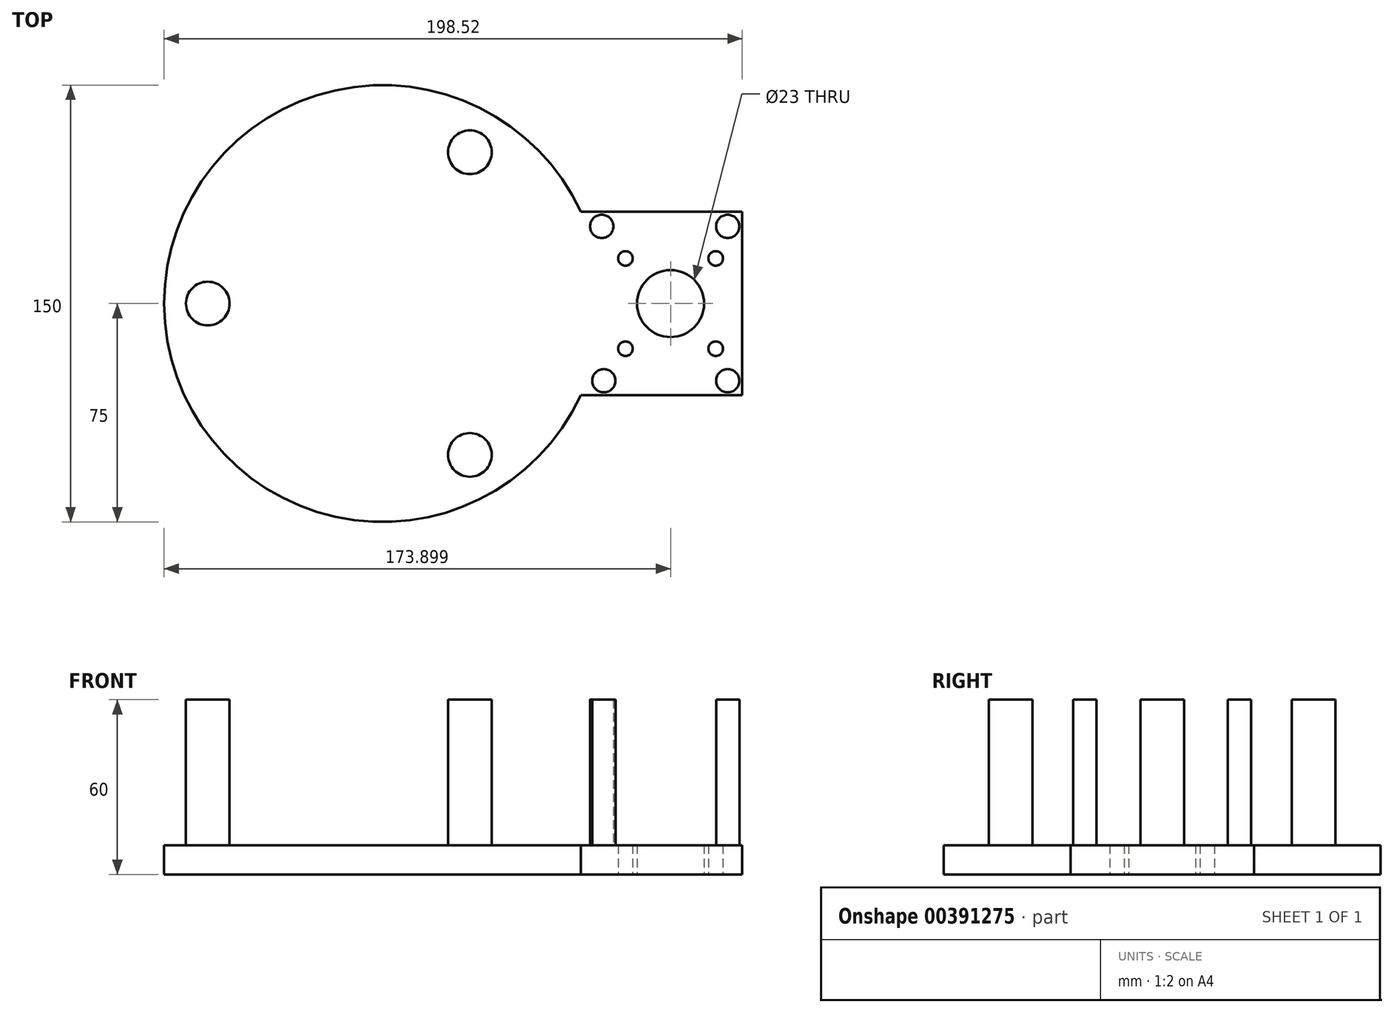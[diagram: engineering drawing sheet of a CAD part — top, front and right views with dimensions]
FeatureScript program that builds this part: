
annotation { "Feature Type Name" : "Feature", "Feature Type Description" : "" }
export const myFeature = defineFeature(function(context is Context, id is Id, definition is map)
    precondition{}
    {
        {
            var Q0;
            Q0=qCreatedBy(makeId("Top.planeOp"),FACE);
            var sketch = newSketch(context, id + "F0", { "sketchPlane" : qUnion([Q0])});
            skCircle(sketch, "E0", {"center": v(0, 0) * mm, "radius": 75 * mm});
            skLineSegment(sketch, "E1.bottom", {"start": v(123.52, -31.5) * mm, "end": v(70.52, -31.5) * mm, "construction": true});
            skLineSegment(sketch, "E1.top", {"start": v(123.52, 31.5) * mm, "end": v(70.52, 31.5) * mm, "construction": true});
            skLineSegment(sketch, "E1.left", {"start": v(123.52, -31.5) * mm, "end": v(123.52, 31.5) * mm, "construction": true});
            skLineSegment(sketch, "E1.right", {"start": v(70.52, -31.5) * mm, "end": v(70.52, 31.5) * mm, "construction": true});
            skPoint(sketch, "E1.middle", {"position": v(97.02, 0) * mm});
            skLineSegment(sketch, "E2", {"start": v(68.06, 31.5) * mm, "end": v(123.52, 31.5) * mm});
            skLineSegment(sketch, "E3", {"start": v(68.06, -31.5) * mm, "end": v(123.52, -31.5) * mm});
            skLineSegment(sketch, "E4", {"start": v(123.52, 31.5) * mm, "end": v(123.52, -31.5) * mm});
            skSolve(sketch);
        }
        {
            var Q0;
            {var subQ0=sQuery(id+"F0.wireOp",EDGE,"E0");var subQ1=makeQuery(id+"F0.imprint","INTERSECT",VERTEX,{"derivedFrom":[subQ0,sQuery(id+"F0.wireOp",EDGE,"E2")]});Q0=makeQuery(id+"F0.imprint","IMPRINT",FACE,{"disambiguationData":[TD([[makeQuery(id+"F0.imprint","IMPRINT",EDGE,{"disambiguationData":[TD([[subQ1,-1.0]])],"derivedFrom":subQ0}),1.0]])]});}
            var Q1;
            {var subQ0=sQuery(id+"F0.wireOp",EDGE,"E2");Q1=makeQuery(id+"F0.imprint","IMPRINT",FACE,{"disambiguationData":[TD([[makeQuery(id+"F0.imprint","IMPRINT",EDGE,{"derivedFrom":subQ0}),-1.0]])]});}
            extrude(context, id + "F1", {"entities" : qUnion([Q0, Q1]), "depth" : 10 * mm});
        }
        {
            var Q0;
            {var subQ0=sQuery(id+"F0.wireOp",EDGE,"E2");Q0=makeQuery(id+"F0.imprint","IMPRINT",FACE,{"disambiguationData":[TD([[makeQuery(id+"F0.imprint","IMPRINT",EDGE,{"derivedFrom":subQ0}),-1.0]])]});}
            var sketch = newSketch(context, id + "F2", { "sketchPlane" : qUnion([Q0])});
            skLineSegment(sketch, "E5.bottom", {"start": v(83.4, -15.5) * mm, "end": v(114.4, -15.5) * mm, "construction": true});
            skLineSegment(sketch, "E5.top", {"start": v(83.4, 15.5) * mm, "end": v(114.4, 15.5) * mm, "construction": true});
            skLineSegment(sketch, "E5.left", {"start": v(83.4, -15.5) * mm, "end": v(83.4, 15.5) * mm, "construction": true});
            skLineSegment(sketch, "E5.right", {"start": v(114.4, -15.5) * mm, "end": v(114.4, 15.5) * mm, "construction": true});
            skPoint(sketch, "E5.middle", {"position": v(98.9, 0) * mm});
            skCircle(sketch, "E6", {"center": v(114.4, 15.5) * mm, "radius": 2.5 * mm});
            skCircle(sketch, "E7", {"center": v(83.4, 15.5) * mm, "radius": 2.5 * mm});
            skCircle(sketch, "E8", {"center": v(83.4, -15.5) * mm, "radius": 2.5 * mm});
            skCircle(sketch, "E9", {"center": v(114.4, -15.5) * mm, "radius": 2.5 * mm});
            skCircle(sketch, "E10", {"center": v(98.9, 0) * mm, "radius": 11.5 * mm});
            skSolve(sketch);
        }
        {
            var Q0;
            Q0=makeQuery(id+"F2.imprint","IMPRINT",FACE,{"disambiguationData":[TD([[makeQuery(id+"F2.imprint","IMPRINT",EDGE,{"derivedFrom":sQuery(id+"F2.wireOp",EDGE,"E6")}),1.0]])]});
            var Q1;
            Q1=makeQuery(id+"F2.imprint","IMPRINT",FACE,{"disambiguationData":[TD([[makeQuery(id+"F2.imprint","IMPRINT",EDGE,{"derivedFrom":sQuery(id+"F2.wireOp",EDGE,"E7")}),1.0]])]});
            var Q2;
            Q2=makeQuery(id+"F2.imprint","IMPRINT",FACE,{"disambiguationData":[TD([[makeQuery(id+"F2.imprint","IMPRINT",EDGE,{"derivedFrom":sQuery(id+"F2.wireOp",EDGE,"E8")}),1.0]])]});
            var Q3;
            Q3=makeQuery(id+"F2.imprint","IMPRINT",FACE,{"disambiguationData":[TD([[makeQuery(id+"F2.imprint","IMPRINT",EDGE,{"derivedFrom":sQuery(id+"F2.wireOp",EDGE,"E9")}),1.0]])]});
            var Q4;
            Q4=makeQuery(id+"F1.opExtrude","CAP_FACE",FACE,{"disambiguationData":[OSD([sQuery(id+"F0.wireOp",EDGE,"E0"),sQuery(id+"F0.wireOp",EDGE,"E2"),sQuery(id+"F0.wireOp",EDGE,"E3"),sQuery(id+"F0.wireOp",EDGE,"E4")])],"isStart":false});
            extrude(context, id + "F3", {"entities" : qUnion([Q0, Q1, Q2, Q3]), "operationType" : NewBodyOperationType.REMOVE, "endBound" : BoundingType.UP_TO_SURFACE, "endBoundEntityFace" : qUnion([Q4]), "depth" : 11 * mm});
        }
        {
            var Q0;
            Q0=makeQuery(id+"F2.imprint","IMPRINT",FACE,{"disambiguationData":[TD([[makeQuery(id+"F2.imprint","IMPRINT",EDGE,{"derivedFrom":sQuery(id+"F2.wireOp",EDGE,"E10")}),1.0]])]});
            var Q1;
            Q1=makeQuery(id+"F1.opExtrude","CAP_FACE",FACE,{"disambiguationData":[OSD([sQuery(id+"F0.wireOp",EDGE,"E0"),sQuery(id+"F0.wireOp",EDGE,"E2"),sQuery(id+"F0.wireOp",EDGE,"E3"),sQuery(id+"F0.wireOp",EDGE,"E4")])],"isStart":false});
            extrude(context, id + "F4", {"entities" : qUnion([Q0]), "operationType" : NewBodyOperationType.REMOVE, "endBound" : BoundingType.UP_TO_SURFACE, "endBoundEntityFace" : qUnion([Q1]), "depth" : 25 * mm});
        }
        {
            var Q0;
            Q0=makeQuery(id+"F1.opExtrude","CAP_FACE",FACE,{"disambiguationData":[OSD([sQuery(id+"F0.wireOp",EDGE,"E0"),sQuery(id+"F0.wireOp",EDGE,"E2"),sQuery(id+"F0.wireOp",EDGE,"E3"),sQuery(id+"F0.wireOp",EDGE,"E4")])],"isStart":false});
            var sketch = newSketch(context, id + "F5", { "sketchPlane" : qUnion([Q0])});
            skLineSegment(sketch, "E11.bottom", {"start": v(123.52, -31.5) * mm, "end": v(118.52, -31.5) * mm, "construction": true});
            skLineSegment(sketch, "E11.top", {"start": v(123.52, -26.5) * mm, "end": v(118.52, -26.5) * mm, "construction": true});
            skLineSegment(sketch, "E11.left", {"start": v(123.52, -31.5) * mm, "end": v(123.52, -26.5) * mm, "construction": true});
            skLineSegment(sketch, "E11.right", {"start": v(118.52, -31.5) * mm, "end": v(118.52, -26.5) * mm, "construction": true});
            skLineSegment(sketch, "E12.bottom", {"start": v(123.52, 31.5) * mm, "end": v(118.52, 31.5) * mm, "construction": true});
            skLineSegment(sketch, "E12.top", {"start": v(123.52, 26.5) * mm, "end": v(118.52, 26.5) * mm, "construction": true});
            skLineSegment(sketch, "E12.left", {"start": v(123.52, 31.5) * mm, "end": v(123.52, 26.5) * mm, "construction": true});
            skLineSegment(sketch, "E12.right", {"start": v(118.52, 31.5) * mm, "end": v(118.52, 26.5) * mm, "construction": true});
            skCircle(sketch, "E13", {"center": v(0, 0) * mm, "radius": 60 * mm, "construction": true});
            skLineSegment(sketch, "E14", {"start": v(75.26, 31.5) * mm, "end": v(75.26, 26.5) * mm, "construction": true});
            skLineSegment(sketch, "E15", {"start": v(75.97, -31.5) * mm, "end": v(75.97, -26.5) * mm, "construction": true});
            skCircle(sketch, "E16", {"center": v(-60, 0) * mm, "radius": 7.5 * mm});
            skCircle(sketch, "E17.1.0", {"center": v(30, -51.96) * mm, "radius": 7.5 * mm});
            skCircle(sketch, "E17.2.0", {"center": v(30, 51.96) * mm, "radius": 7.5 * mm});
            skCircle(sketch, "E18", {"center": v(75.26, 26.5) * mm, "radius": 4 * mm});
            skCircle(sketch, "E19", {"center": v(118.52, 26.5) * mm, "radius": 4 * mm});
            skCircle(sketch, "E20", {"center": v(118.52, -26.5) * mm, "radius": 4 * mm});
            skCircle(sketch, "E21", {"center": v(75.97, -26.5) * mm, "radius": 4 * mm});
            skSolve(sketch);
        }
        {
            var Q0;
            Q0=makeQuery(id+"F5.imprint","IMPRINT",FACE,{"disambiguationData":[TD([[makeQuery(id+"F5.imprint","IMPRINT",EDGE,{"derivedFrom":sQuery(id+"F5.wireOp",EDGE,"E16")}),1.0]])]});
            var Q1;
            Q1=makeQuery(id+"F5.imprint","IMPRINT",FACE,{"disambiguationData":[TD([[makeQuery(id+"F5.imprint","IMPRINT",EDGE,{"derivedFrom":sQuery(id+"F5.wireOp",EDGE,"E17.2.0")}),1.0]])]});
            var Q2;
            Q2=makeQuery(id+"F5.imprint","IMPRINT",FACE,{"disambiguationData":[TD([[makeQuery(id+"F5.imprint","IMPRINT",EDGE,{"derivedFrom":sQuery(id+"F5.wireOp",EDGE,"E17.1.0")}),1.0]])]});
            var Q3;
            Q3=makeQuery(id+"F5.imprint","IMPRINT",FACE,{"disambiguationData":[TD([[makeQuery(id+"F5.imprint","IMPRINT",EDGE,{"derivedFrom":sQuery(id+"F5.wireOp",EDGE,"E21")}),1.0]])]});
            var Q4;
            Q4=makeQuery(id+"F5.imprint","IMPRINT",FACE,{"disambiguationData":[TD([[makeQuery(id+"F5.imprint","IMPRINT",EDGE,{"derivedFrom":sQuery(id+"F5.wireOp",EDGE,"E20")}),1.0]])]});
            var Q5;
            Q5=makeQuery(id+"F5.imprint","IMPRINT",FACE,{"disambiguationData":[TD([[makeQuery(id+"F5.imprint","IMPRINT",EDGE,{"derivedFrom":sQuery(id+"F5.wireOp",EDGE,"E18")}),1.0]])]});
            var Q6;
            Q6=makeQuery(id+"F5.imprint","IMPRINT",FACE,{"disambiguationData":[TD([[makeQuery(id+"F5.imprint","IMPRINT",EDGE,{"derivedFrom":sQuery(id+"F5.wireOp",EDGE,"E19")}),1.0]])]});
            extrude(context, id + "F6", {"entities" : qUnion([Q0, Q1, Q2, Q3, Q4, Q5, Q6]), "operationType" : NewBodyOperationType.ADD, "depth" : 50 * mm});
        }
        {
            var Q0;
            Q0=makeQuery(id+"F5.imprint","IMPRINT",FACE,{"disambiguationData":[TD([[makeQuery(id+"F5.imprint","IMPRINT",EDGE,{"derivedFrom":sQuery(id+"F5.wireOp",EDGE,"E16")}),-1.0]])]});
            cPlane(context, id + "F7", {"entities" : qUnion([Q0]), "cplaneType" : CPlaneType.OFFSET, "offset" : 10 * mm, "oppositeDirection" : true, "width" : 150 * mm, "height" : 150 * mm});
        }
    });
